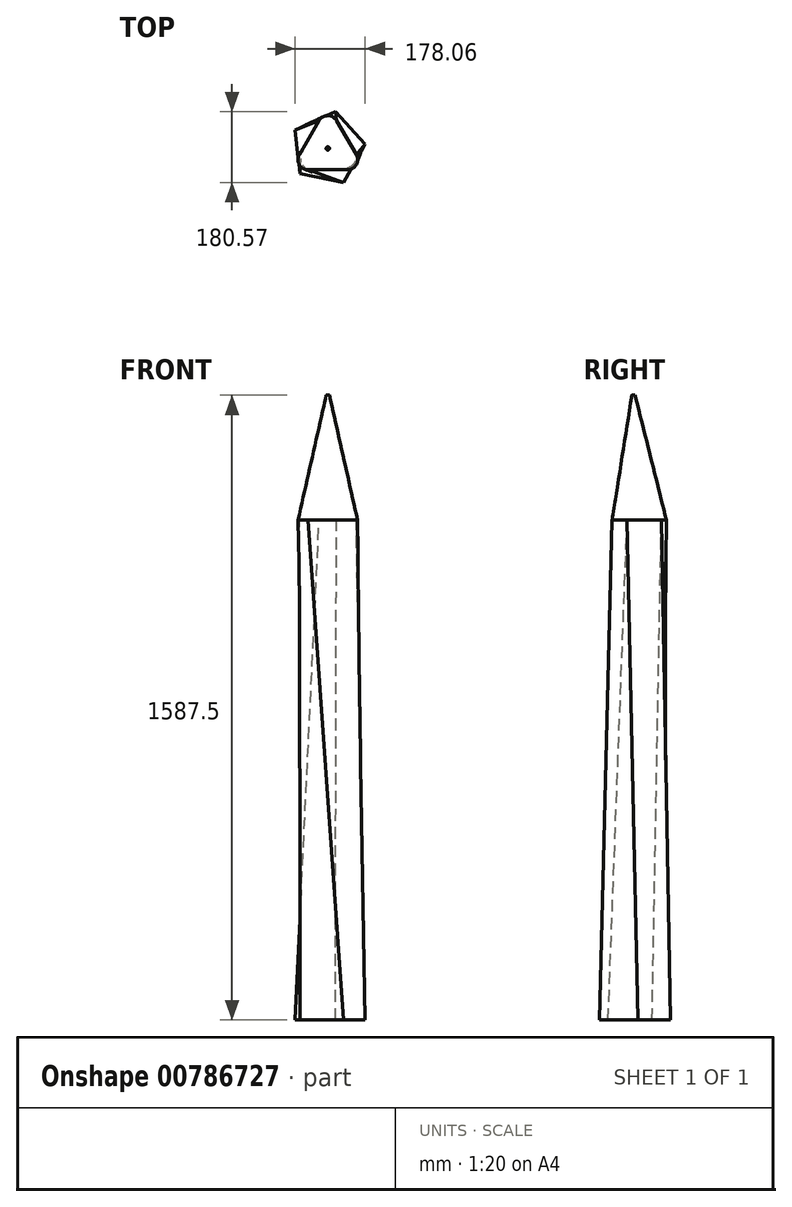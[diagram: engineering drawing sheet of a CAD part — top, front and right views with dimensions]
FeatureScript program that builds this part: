
annotation { "Feature Type Name" : "Feature", "Feature Type Description" : "" }
export const myFeature = defineFeature(function(context is Context, id is Id, definition is map)
    precondition{}
    {
        {
            var Q0;
            Q0=qCreatedBy(makeId("Top.planeOp"),FACE);
            var sketch = newSketch(context, id + "F0", { "sketchPlane" : qUnion([Q0])});
            skCircle(sketch, "E0.cCircle", {"center": v(0, 0) * mm, "radius": 54.44 * mm, "construction": true});
            skLineSegment(sketch, "E0.0", {"start": v(21.99, 70.79) * mm, "end": v(72.3, -16.33) * mm});
            skLineSegment(sketch, "E0.1", {"start": v(50.3, -54.43) * mm, "end": v(-50.3, -54.45) * mm});
            skLineSegment(sketch, "E0.2", {"start": v(-72.3, -16.35) * mm, "end": v(-22, 70.78) * mm});
            skPoint(sketch, "E0.0.midPoint", {"position": v(47.14, 27.23) * mm});
            skPoint(sketch, "E1.visualSharp", {"position": v(-0.01, 108.88) * mm});
            skArc(sketch, "E1.filletArc", {"start": v(21.99, 70.79) * mm, "mid": v(-0.01, 83.48) * mm, "end": v(-22, 70.78) * mm});
            skPoint(sketch, "E2.visualSharp", {"position": v(-94.29, -54.45) * mm});
            skArc(sketch, "E2.filletArc", {"start": v(-72.3, -16.35) * mm, "mid": v(-72.3, -41.75) * mm, "end": v(-50.3, -54.45) * mm});
            skPoint(sketch, "E3.visualSharp", {"position": v(94.3, -54.43) * mm});
            skArc(sketch, "E3.filletArc", {"start": v(50.3, -54.43) * mm, "mid": v(72.3, -41.73) * mm, "end": v(72.3, -16.33) * mm});
            skSolve(sketch);
        }
        {
            var Q0;
            Q0=qCreatedBy(makeId("Top.planeOp"),FACE);
            var Q1;
            Q1 = qBodyType(qCreatedBy(id + "F2" ,EDGE), BodyType.WIRE);
            cPlane(context, id + "F1", {"entities" : qUnion([Q0, Q1]), "cplaneType" : CPlaneType.OFFSET, "offset" : 317.5 * mm, "width" : 152.4 * mm, "height" : 152.4 * mm});
        }
        {
            var Q0;
            Q0=qCreatedBy(id+"F1.planeOp",FACE);
            var sketch = newSketch(context, id + "F2", { "sketchPlane" : qUnion([Q0])});
            skCircle(sketch, "E4", {"center": v(0, 0) * mm, "radius": 4.13 * mm});
            skSolve(sketch);
        }
        {
            var Q0;
            Q0=makeQuery(id+"F2.imprint","IMPRINT",FACE,{"disambiguationData":[TD([[makeQuery(id+"F2.imprint","IMPRINT",EDGE,{"derivedFrom":sQuery(id+"F2.wireOp",EDGE,"E4")}),1.0]])]});
            var Q1;
            Q1=makeQuery(id+"F0.imprint","IMPRINT",FACE,{"disambiguationData":[TD([[makeQuery(id+"F0.imprint","IMPRINT",EDGE,{"derivedFrom":sQuery(id+"F0.wireOp",EDGE,"E0.0")}),-1.0]])]});
            loft(context, id + "F3", {"sheetProfilesArray" : [{ "sheetProfileEntities" : qUnion([Q0]) }, { "sheetProfileEntities" : qUnion([Q1]) }]});
        }
        {
            var Q0;
            Q0=qCreatedBy(makeId("Top.planeOp"),FACE);
            cPlane(context, id + "F4", {"entities" : qUnion([Q0]), "cplaneType" : CPlaneType.OFFSET, "offset" : 1270 * mm, "oppositeDirection" : true, "width" : 152.4 * mm, "height" : 152.4 * mm});
        }
        {
            var Q0;
            Q0=qCreatedBy(id+"F4.planeOp",FACE);
            var sketch = newSketch(context, id + "F5", { "sketchPlane" : qUnion([Q0])});
            skCircle(sketch, "E5.cCircle", {"center": v(0, 0) * mm, "radius": 77.3 * mm, "construction": true});
            skLineSegment(sketch, "E5.0", {"start": v(94.93, 10.76) * mm, "end": v(39.57, -86.96) * mm});
            skLineSegment(sketch, "E5.1", {"start": v(39.57, -86.96) * mm, "end": v(-70.48, -64.5) * mm});
            skLineSegment(sketch, "E5.2", {"start": v(-70.48, -64.5) * mm, "end": v(-83.13, 47.1) * mm});
            skLineSegment(sketch, "E5.3", {"start": v(-83.13, 47.1) * mm, "end": v(19.1, 93.61) * mm});
            skLineSegment(sketch, "E5.4", {"start": v(19.1, 93.61) * mm, "end": v(94.93, 10.76) * mm});
            skPoint(sketch, "E5.0.midPoint", {"position": v(67.25, -38.1) * mm});
            skSolve(sketch);
        }
        {
            var Q1;
            Q1=makeQuery(id+"F5.imprint","IMPRINT",FACE,{"disambiguationData":[TD([[makeQuery(id+"F5.imprint","IMPRINT",EDGE,{"derivedFrom":sQuery(id+"F5.wireOp",EDGE,"E5.0")}),-1.0]])]});
            var Q2;
            Q2=makeQuery(id+"F0.imprint","IMPRINT",FACE,{"disambiguationData":[TD([[makeQuery(id+"F0.imprint","IMPRINT",EDGE,{"derivedFrom":sQuery(id+"F0.wireOp",EDGE,"E0.0")}),-1.0]])]});
            loft(context, id + "F6", {"operationType" : NewBodyOperationType.ADD, "sheetProfilesArray" : [{ "sheetProfileEntities" : qUnion([Q1]) }, { "sheetProfileEntities" : qUnion([Q2]) }]});
        }
    });
